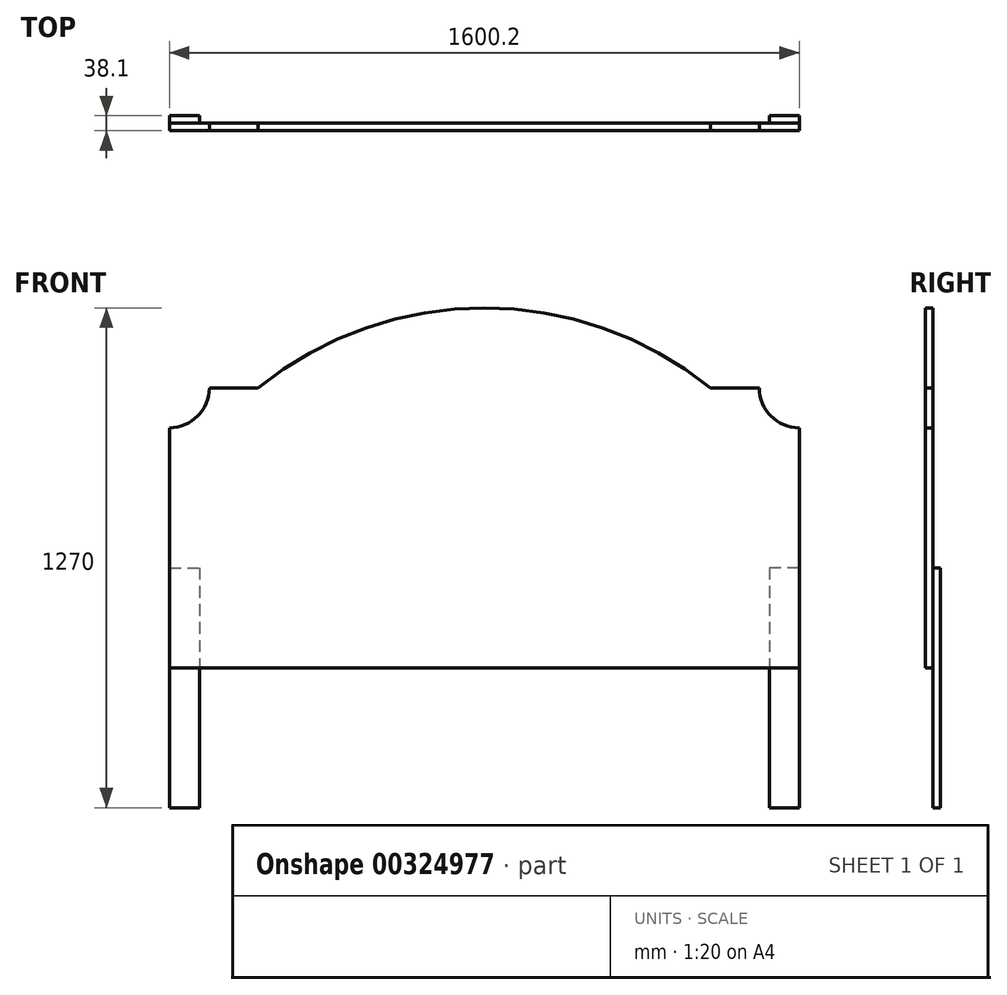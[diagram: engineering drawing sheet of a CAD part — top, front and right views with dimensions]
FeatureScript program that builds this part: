
annotation { "Feature Type Name" : "Feature", "Feature Type Description" : "" }
export const myFeature = defineFeature(function(context is Context, id is Id, definition is map)
    precondition{}
    {
        {
            var Q0;
            Q0=qCreatedBy(makeId("Front.planeOp"),FACE);
            var sketch = newSketch(context, id + "F0", { "sketchPlane" : qUnion([Q0])});
            skLineSegment(sketch, "E0.bottom", {"start": v(0, 0) * mm, "end": v(800.1, 0) * mm});
            skLineSegment(sketch, "E0.top", {"start": v(0, 914.4) * mm, "end": v(800.1, 914.4) * mm, "construction": true});
            skLineSegment(sketch, "E0.left", {"start": v(0, 0) * mm, "end": v(0, 914.4) * mm, "construction": true});
            skLineSegment(sketch, "E0.right", {"start": v(800.1, 0) * mm, "end": v(800.1, 609.6) * mm});
            skArc(sketch, "E1", {"start": v(0, 914.4) * mm, "mid": v(304.8, 862.1) * mm, "end": v(574.74, 711.2) * mm});
            skLineSegment(sketch, "E2", {"start": v(574.74, 711.2) * mm, "end": v(698.5, 711.2) * mm});
            skArc(sketch, "E3", {"start": v(698.5, 711.2) * mm, "mid": v(728.26, 639.36) * mm, "end": v(800.1, 609.6) * mm});
            skArc(sketch, "E4.MirrorCS", {"start": v(0, 914.4) * mm, "mid": v(-304.8, 862.1) * mm, "end": v(-574.74, 711.2) * mm});
            skLineSegment(sketch, "E5.MirrorCS", {"start": v(-574.74, 711.2) * mm, "end": v(-698.5, 711.2) * mm});
            skArc(sketch, "E6.MirrorCS", {"start": v(-698.5, 711.2) * mm, "mid": v(-728.26, 639.36) * mm, "end": v(-800.1, 609.6) * mm});
            skLineSegment(sketch, "E7.MirrorCS", {"start": v(-800.1, 0) * mm, "end": v(-800.1, 609.6) * mm});
            skLineSegment(sketch, "E8.MirrorCS", {"start": v(0, 0) * mm, "end": v(-800.1, 0) * mm});
            skSolve(sketch);
        }
        {
            var Q0;
            Q0 = qSketchRegion(id + "F0", true);
            extrude(context, id + "F1", {"entities" : qUnion([Q0]), "depth" : 19.05 * mm});
        }
        {
            var Q0;
            Q0=makeQuery(id+"F1.opExtrude","CAP_FACE",FACE,{"disambiguationData":[OSD([sQuery(id+"F0.wireOp",EDGE,"E0.bottom"),sQuery(id+"F0.wireOp",EDGE,"E0.right"),sQuery(id+"F0.wireOp",EDGE,"E1"),sQuery(id+"F0.wireOp",EDGE,"E2"),sQuery(id+"F0.wireOp",EDGE,"E3"),sQuery(id+"F0.wireOp",EDGE,"E4.MirrorCS"),sQuery(id+"F0.wireOp",EDGE,"E5.MirrorCS"),sQuery(id+"F0.wireOp",EDGE,"E6.MirrorCS"),sQuery(id+"F0.wireOp",EDGE,"E7.MirrorCS"),sQuery(id+"F0.wireOp",EDGE,"E8.MirrorCS")])],"isStart":true});
            var sketch = newSketch(context, id + "F2", { "sketchPlane" : qUnion([Q0])});
            skLineSegment(sketch, "E9.bottom", {"start": v(-800.1, 254) * mm, "end": v(-723.9, 254) * mm});
            skLineSegment(sketch, "E9.top", {"start": v(-800.1, -355.6) * mm, "end": v(-723.9, -355.6) * mm});
            skLineSegment(sketch, "E9.left", {"start": v(-800.1, 254) * mm, "end": v(-800.1, -355.6) * mm});
            skLineSegment(sketch, "E9.right", {"start": v(-723.9, 254) * mm, "end": v(-723.9, -355.6) * mm});
            skSolve(sketch);
        }
        {
            var Q0;
            Q0 = qSketchRegion(id + "F2", true);
            extrude(context, id + "F3", {"entities" : qUnion([Q0]), "depth" : 19.05 * mm});
        }
        {
            var Q0;
            Q0=makeQuery(id+"F3.opExtrude","SWEPT_BODY",BODY,{"disambiguationData":[OSD([sQuery(id+"F2.wireOp",EDGE,"E9.bottom"),sQuery(id+"F2.wireOp",EDGE,"E9.top"),sQuery(id+"F2.wireOp",EDGE,"E9.left"),sQuery(id+"F2.wireOp",EDGE,"E9.right")])]});
            var Q1;
            Q1=qCreatedBy(makeId("Right.planeOp"),FACE);
            mirror(context, id + "F4", {"entities" : qUnion([Q0]), "mirrorPlane" : qUnion([Q1])});
        }
    });
